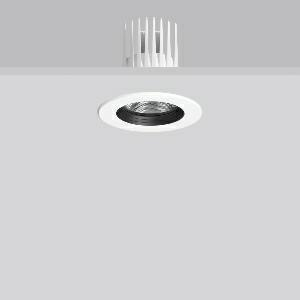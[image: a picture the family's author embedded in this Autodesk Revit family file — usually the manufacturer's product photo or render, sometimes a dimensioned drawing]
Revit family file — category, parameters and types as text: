
# Revit family: heledon_mini_e_901748_002_3_dbf3
name_source: partatom
category: Lighting Fixtures
units: mm (PartAtom-declared; Revit-internal decimal feet)

## family parameters
Cut with Voids When Loaded = No
Host = Face
Light Source = No
Part Type = Normal
Room Calculation Point = No
Round Connector Dimension = Use Diameter
Shared = No

## types (1)
- HELEDON mini E (1 x LED Modul 935, 3700 lm, 3500)
    Apparent Load = 29 VA
    Approval mark = CE
    CIE Flux Codes = 100 100 100 100 100
    Color Rendering = 92
    Color Temperature = 3500
    Default Elevation = 1800 mm
    Description = Series: HELEDON mini
Round recessed downlight. Housing: die-cast aluminium, powder-coated. Black plastic ring and recessed LED to prevent glare from the side. Optical assembly with reflector made of MIRO-Silver with 98% total light reflection for outstanding efficiency - can be changed without tools. Best colour rendering index Ra>90. Suitable for Recessed ceiling mounting. Installation without tools thanks to spring fastening system. Including separate LED converter with connecting cable 600 mm.High quality converter without flickering and stroboscopic effect. Through-wiring box (5 pole) available as accessory. The following accessories can be mounted without use of tools: interchangeable lenses, decorative glasses, honeycomb louvre, clear and frosted diffusers, white interchangeable plastic ring. 
Colour: traffic white, matt (RAL 9016)
Diameter: 124 mm
Height: 3 mm
Cut-out diameter: 114 mm
Recess height: 170 mm
Luminaire: recess height: 120 mm
Lamp: LED
Socket: without socket
Colour temperature: 3500K
Colour rendering index (CRI): 92
System power: 29 W
Rated luminous flux: 3700 lm
Luminous efficiency: 128 lm/W
Control gear: Regulated power supply
Protection class: II
Type of protection: IP 20
    Height = 0 mm  [stored 0 ft]
    Lamp = 1 x LED Modul 935
    Lamp Light Flux = 3700 lm
    Lamp count = 1
    Length = 124 mm  [stored 0.406824 ft]
    Lifetime = 50000 h
    Luminous efficacy = 128 lm/W
    Manufacturer = RZB
    ModVariant = No
    Model = 901748.002.3
    Mounting Place = Ceiling
    Mounting Type = Recessed
    Number of Poles = 1
    OnlyDefault = Yes
    Power Factor = 1
    Product Name = HELEDON mini E
    Product group = Recessed downlights
    ProductGroupID = 402
    Protection Class = Protection class II
    Protection Degree = IP 20
    RLX_Detail_Level = 1
    RLX_Emergency_Light_Flux = 0 lm
    RLX_Emergency_Type = 0
    RLX_Emergency_Type_DB = No
    RlxData = <blob elided: 125769 chars, md5=307dd6b4>
    Socket = socket
    Standby Power = 0 W
    System Light Flux = 3700 lm
    System Power = 29 W
    Type Comments = Product without accessories
    Type Image = 901657.002.jpg
    URL = http://relux.com
    VarID = ---
    Voltage = 230 V
    Voltage Range = 220-240 V
    Weight = 0.00 kg
    Width = 0 mm  [stored 0 ft]

note: [stored X ft] marks values corroborated as IEEE doubles in the binary element streams (Revit-internal decimal feet)

## geometry (parser evidence)
native form markers: Blend x4, Sweep x11
no freeform markers — native parametric forms only
